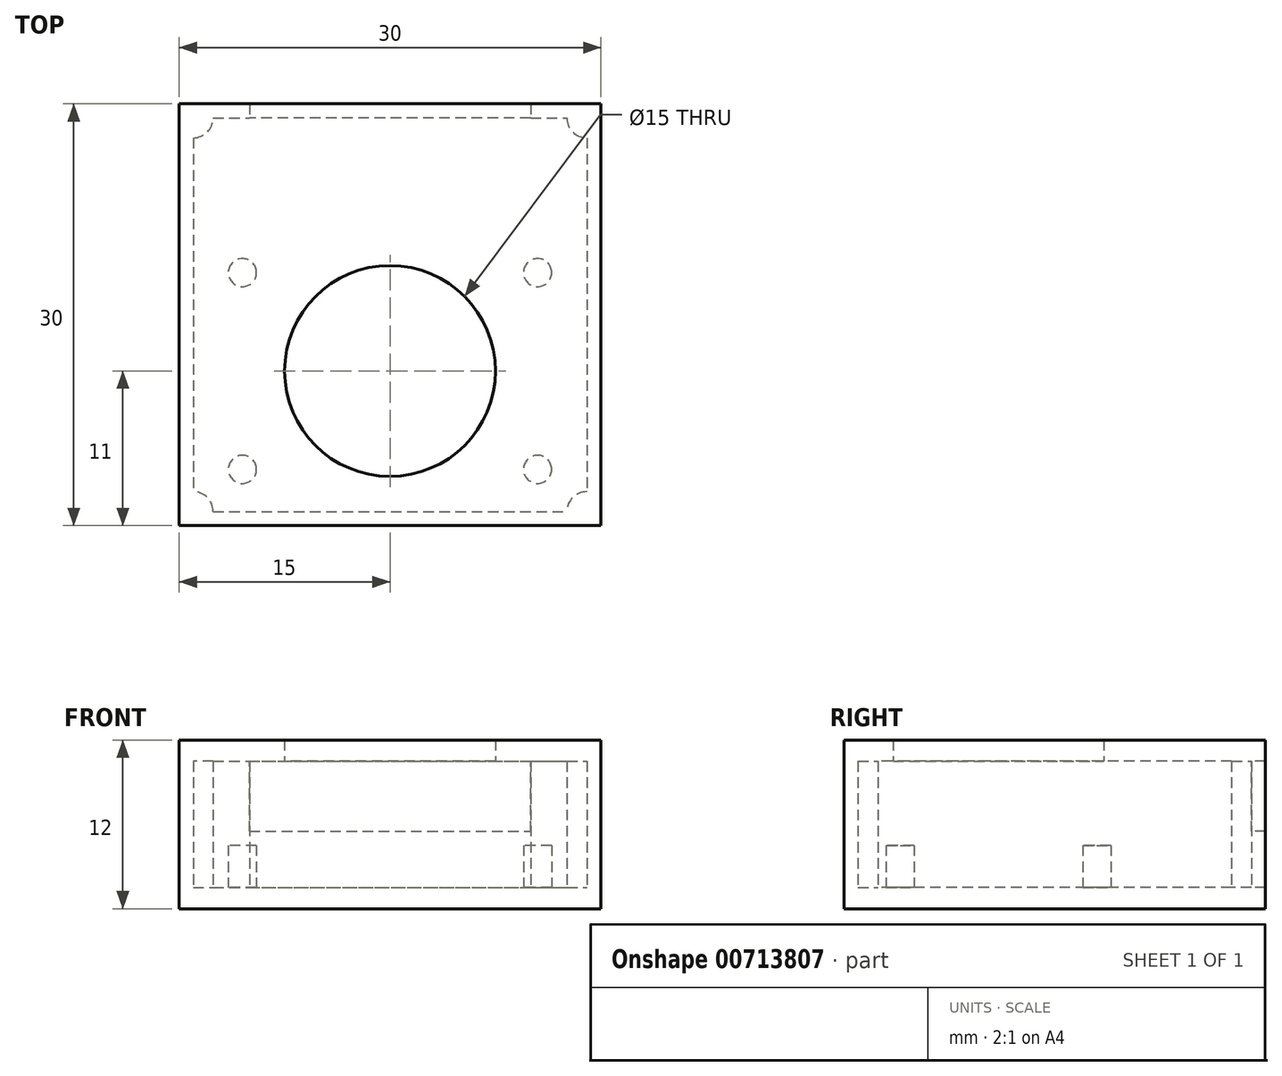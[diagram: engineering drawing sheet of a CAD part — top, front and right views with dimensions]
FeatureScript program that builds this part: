
annotation { "Feature Type Name" : "Feature", "Feature Type Description" : "" }
export const myFeature = defineFeature(function(context is Context, id is Id, definition is map)
    precondition{}
    {
        {
            var Q0;
            Q0=qCreatedBy(makeId("Top.planeOp"),FACE);
            var sketch = newSketch(context, id + "F0", { "sketchPlane" : qUnion([Q0])});
            skLineSegment(sketch, "E0.bottom", {"start": v(0, 0) * mm, "end": v(30, 0) * mm});
            skLineSegment(sketch, "E0.top", {"start": v(0, -30) * mm, "end": v(30, -30) * mm});
            skLineSegment(sketch, "E0.left", {"start": v(0, 0) * mm, "end": v(0, -30) * mm});
            skLineSegment(sketch, "E0.right", {"start": v(30, 0) * mm, "end": v(30, -30) * mm});
            skLineSegment(sketch, "E1.0", {"start": v(1, -1) * mm, "end": v(29, -1) * mm});
            skLineSegment(sketch, "E1.1", {"start": v(1, -1) * mm, "end": v(1, -29) * mm});
            skLineSegment(sketch, "E1.2", {"start": v(1, -29) * mm, "end": v(29, -29) * mm});
            skLineSegment(sketch, "E1.3", {"start": v(29, -1) * mm, "end": v(29, -29) * mm});
            skLineSegment(sketch, "E2", {"start": v(15, -29) * mm, "end": v(15, -1) * mm, "construction": true});
            skPoint(sketch, "E3.start.orphan", {"position": v(1, -19) * mm});
            skPoint(sketch, "E4.start.orphan", {"position": v(29, -19) * mm});
            skLineSegment(sketch, "E5", {"start": v(1, -19) * mm, "end": v(29, -19) * mm, "construction": true});
            skLineSegment(sketch, "E6", {"start": v(1, -12) * mm, "end": v(29, -12) * mm, "construction": true});
            skLineSegment(sketch, "E7", {"start": v(1, -26) * mm, "end": v(29, -26) * mm, "construction": true});
            skLineSegment(sketch, "E8", {"start": v(25.5, -1) * mm, "end": v(25.5, -29) * mm, "construction": true});
            skLineSegment(sketch, "E9", {"start": v(4.5, -1) * mm, "end": v(4.5, -29) * mm, "construction": true});
            skCircle(sketch, "E10", {"center": v(25.5, -12) * mm, "radius": 1 * mm});
            skCircle(sketch, "E11", {"center": v(4.5, -12) * mm, "radius": 1 * mm});
            skCircle(sketch, "E12", {"center": v(4.5, -26) * mm, "radius": 1 * mm});
            skCircle(sketch, "E13", {"center": v(25.5, -26) * mm, "radius": 1 * mm});
            skLineSegment(sketch, "E14", {"start": v(5, 0) * mm, "end": v(5, -1) * mm});
            skLineSegment(sketch, "E15", {"start": v(25, 0) * mm, "end": v(25, -1) * mm});
            skCircle(sketch, "E16", {"center": v(1, -29) * mm, "radius": 1.41 * mm});
            skCircle(sketch, "E17", {"center": v(29, -29) * mm, "radius": 1.41 * mm});
            skCircle(sketch, "E18", {"center": v(29, -1) * mm, "radius": 1.41 * mm});
            skCircle(sketch, "E19", {"center": v(1, -1) * mm, "radius": 1.41 * mm});
            skSolve(sketch);
        }
        {
            var Q0;
            {var subQ0=sQuery(id+"F0.wireOp",EDGE,"E1.1");Q0=makeQuery(id+"F0.imprint","IMPRINT",FACE,{"disambiguationData":[TD([[makeQuery(id+"F0.imprint","IMPRINT",EDGE,{"derivedFrom":subQ0}),1.0]])]});}
            var Q1;
            Q1=makeQuery(id+"F0.imprint","IMPRINT",FACE,{"disambiguationData":[TD([[makeQuery(id+"F0.imprint","IMPRINT",EDGE,{"derivedFrom":sQuery(id+"F0.wireOp",EDGE,"E0.top")}),1.0]])]});
            var Q2;
            Q2=makeQuery(id+"F0.imprint","IMPRINT",FACE,{"disambiguationData":[TD([[makeQuery(id+"F0.imprint","IMPRINT",EDGE,{"derivedFrom":sQuery(id+"F0.wireOp",EDGE,"E11")}),1.0]])]});
            var Q3;
            Q3=makeQuery(id+"F0.imprint","IMPRINT",FACE,{"disambiguationData":[TD([[makeQuery(id+"F0.imprint","IMPRINT",EDGE,{"derivedFrom":sQuery(id+"F0.wireOp",EDGE,"E12")}),1.0]])]});
            var Q4;
            Q4=makeQuery(id+"F0.imprint","IMPRINT",FACE,{"disambiguationData":[TD([[makeQuery(id+"F0.imprint","IMPRINT",EDGE,{"derivedFrom":sQuery(id+"F0.wireOp",EDGE,"E13")}),1.0]])]});
            var Q5;
            Q5=makeQuery(id+"F0.imprint","IMPRINT",FACE,{"disambiguationData":[TD([[makeQuery(id+"F0.imprint","IMPRINT",EDGE,{"derivedFrom":sQuery(id+"F0.wireOp",EDGE,"E10")}),1.0]])]});
            var Q6;
            {var subQ0=sQuery(id+"F0.wireOp",EDGE,"E1.2");var subQ1=sQuery(id+"F0.wireOp",EDGE,"E1.1");var subQ2=makeQuery(id+"F0.imprint","INTERSECT",VERTEX,{"derivedFrom":[subQ1,subQ0]});Q6=makeQuery(id+"F0.imprint","IMPRINT",FACE,{"disambiguationData":[TD([[makeQuery(id+"F0.imprint","IMPRINT",EDGE,{"disambiguationData":[TD([[subQ2,1.0]])],"derivedFrom":subQ1}),-1.0]])]});}
            var Q7;
            {var subQ0=sQuery(id+"F0.wireOp",EDGE,"E19");var subQ1=sQuery(id+"F0.wireOp",EDGE,"E0.left");var subQ2=makeQuery(id+"F0.imprint","INTERSECT",VERTEX,{"derivedFrom":[subQ1,subQ0]});Q7=makeQuery(id+"F0.imprint","IMPRINT",FACE,{"disambiguationData":[TD([[makeQuery(id+"F0.imprint","IMPRINT",EDGE,{"disambiguationData":[TD([[subQ2,-1.0]])],"derivedFrom":subQ1}),1.0]])]});}
            var Q8;
            {var subQ0=sQuery(id+"F0.wireOp",EDGE,"E1.1");var subQ1=sQuery(id+"F0.wireOp",EDGE,"E1.0");var subQ2=makeQuery(id+"F0.imprint","INTERSECT",VERTEX,{"derivedFrom":[subQ1,subQ0]});Q8=makeQuery(id+"F0.imprint","IMPRINT",FACE,{"disambiguationData":[TD([[makeQuery(id+"F0.imprint","IMPRINT",EDGE,{"disambiguationData":[TD([[subQ2,-1.0]])],"derivedFrom":subQ1}),1.0]])]});}
            var Q9;
            {var subQ0=sQuery(id+"F0.wireOp",EDGE,"E14");Q9=makeQuery(id+"F0.imprint","IMPRINT",FACE,{"disambiguationData":[TD([[makeQuery(id+"F0.imprint","IMPRINT",EDGE,{"derivedFrom":subQ0}),1.0]])]});}
            var Q10;
            {var subQ0=sQuery(id+"F0.wireOp",EDGE,"E1.3");var subQ1=sQuery(id+"F0.wireOp",EDGE,"E1.0");var subQ2=makeQuery(id+"F0.imprint","INTERSECT",VERTEX,{"derivedFrom":[subQ1,subQ0]});Q10=makeQuery(id+"F0.imprint","IMPRINT",FACE,{"disambiguationData":[TD([[makeQuery(id+"F0.imprint","IMPRINT",EDGE,{"disambiguationData":[TD([[subQ2,1.0]])],"derivedFrom":subQ1}),1.0]])]});}
            var Q11;
            {var subQ0=sQuery(id+"F0.wireOp",EDGE,"E15");Q11=makeQuery(id+"F0.imprint","IMPRINT",FACE,{"disambiguationData":[TD([[makeQuery(id+"F0.imprint","IMPRINT",EDGE,{"derivedFrom":subQ0}),1.0]])]});}
            var Q12;
            {var subQ0=sQuery(id+"F0.wireOp",EDGE,"E18");var subQ1=sQuery(id+"F0.wireOp",EDGE,"E0.right");var subQ2=makeQuery(id+"F0.imprint","INTERSECT",VERTEX,{"derivedFrom":[subQ1,subQ0]});Q12=makeQuery(id+"F0.imprint","IMPRINT",FACE,{"disambiguationData":[TD([[makeQuery(id+"F0.imprint","IMPRINT",EDGE,{"disambiguationData":[TD([[subQ2,-1.0]])],"derivedFrom":subQ1}),-1.0]])]});}
            var Q13;
            {var subQ0=sQuery(id+"F0.wireOp",EDGE,"E1.3");var subQ1=sQuery(id+"F0.wireOp",EDGE,"E1.2");var subQ2=makeQuery(id+"F0.imprint","INTERSECT",VERTEX,{"derivedFrom":[subQ1,subQ0]});Q13=makeQuery(id+"F0.imprint","IMPRINT",FACE,{"disambiguationData":[TD([[makeQuery(id+"F0.imprint","IMPRINT",EDGE,{"disambiguationData":[TD([[subQ2,1.0]])],"derivedFrom":subQ1}),-1.0]])]});}
            var Q14;
            Q14=makeQuery(id+"F0.imprint","IMPRINT",FACE,{"disambiguationData":[TD([[makeQuery(id+"F0.imprint","IMPRINT",EDGE,{"derivedFrom":sQuery(id+"F0.wireOp",EDGE,"E10")}),-1.0]])]});
            var Q15;
            {var subQ0=sQuery(id+"F0.wireOp",EDGE,"E1.3");var subQ1=sQuery(id+"F0.wireOp",EDGE,"E1.2");var subQ2=makeQuery(id+"F0.imprint","INTERSECT",VERTEX,{"derivedFrom":[subQ1,subQ0]});Q15=makeQuery(id+"F0.imprint","IMPRINT",FACE,{"disambiguationData":[TD([[makeQuery(id+"F0.imprint","IMPRINT",EDGE,{"disambiguationData":[TD([[subQ2,1.0]])],"derivedFrom":subQ1}),1.0]])]});}
            var Q16;
            {var subQ0=sQuery(id+"F0.wireOp",EDGE,"E14");Q16=makeQuery(id+"F0.imprint","IMPRINT",FACE,{"disambiguationData":[TD([[makeQuery(id+"F0.imprint","IMPRINT",EDGE,{"derivedFrom":subQ0}),-1.0]])]});}
            var Q17;
            {var subQ0=sQuery(id+"F0.wireOp",EDGE,"E1.3");var subQ1=sQuery(id+"F0.wireOp",EDGE,"E1.0");var subQ2=makeQuery(id+"F0.imprint","INTERSECT",VERTEX,{"derivedFrom":[subQ1,subQ0]});Q17=makeQuery(id+"F0.imprint","IMPRINT",FACE,{"disambiguationData":[TD([[makeQuery(id+"F0.imprint","IMPRINT",EDGE,{"disambiguationData":[TD([[subQ2,1.0]])],"derivedFrom":subQ1}),-1.0]])]});}
            extrude(context, id + "F1", {"entities" : qUnion([Q0, Q1, Q2, Q3, Q4, Q5, Q6, Q7, Q8, Q9, Q10, Q11, Q12, Q13, Q14, Q15, Q16, Q17]), "oppositeDirection" : true, "depth" : 1.5 * mm, "offsetDistance" : 25 * mm});
        }
        {
            var Q0;
            Q0=makeQuery(id+"F0.imprint","IMPRINT",FACE,{"disambiguationData":[TD([[makeQuery(id+"F0.imprint","IMPRINT",EDGE,{"derivedFrom":sQuery(id+"F0.wireOp",EDGE,"E11")}),1.0]])]});
            var Q1;
            Q1=makeQuery(id+"F0.imprint","IMPRINT",FACE,{"disambiguationData":[TD([[makeQuery(id+"F0.imprint","IMPRINT",EDGE,{"derivedFrom":sQuery(id+"F0.wireOp",EDGE,"E10")}),1.0]])]});
            var Q2;
            Q2=makeQuery(id+"F0.imprint","IMPRINT",FACE,{"disambiguationData":[TD([[makeQuery(id+"F0.imprint","IMPRINT",EDGE,{"derivedFrom":sQuery(id+"F0.wireOp",EDGE,"E13")}),1.0]])]});
            var Q3;
            Q3=makeQuery(id+"F0.imprint","IMPRINT",FACE,{"disambiguationData":[TD([[makeQuery(id+"F0.imprint","IMPRINT",EDGE,{"derivedFrom":sQuery(id+"F0.wireOp",EDGE,"E12")}),1.0]])]});
            extrude(context, id + "F2", {"entities" : qUnion([Q0, Q1, Q2, Q3]), "operationType" : NewBodyOperationType.ADD, "depth" : 3 * mm, "offsetDistance" : 25 * mm});
        }
        {
            var Q0;
            Q0=makeQuery(id+"F0.imprint","IMPRINT",FACE,{"disambiguationData":[TD([[makeQuery(id+"F0.imprint","IMPRINT",EDGE,{"derivedFrom":sQuery(id+"F0.wireOp",EDGE,"E0.top")}),1.0]])]});
            var Q1;
            {var subQ0=sQuery(id+"F0.wireOp",EDGE,"E1.3");var subQ1=sQuery(id+"F0.wireOp",EDGE,"E1.2");var subQ2=makeQuery(id+"F0.imprint","INTERSECT",VERTEX,{"derivedFrom":[subQ1,subQ0]});Q1=makeQuery(id+"F0.imprint","IMPRINT",FACE,{"disambiguationData":[TD([[makeQuery(id+"F0.imprint","IMPRINT",EDGE,{"disambiguationData":[TD([[subQ2,1.0]])],"derivedFrom":subQ1}),-1.0]])]});}
            var Q2;
            {var subQ0=sQuery(id+"F0.wireOp",EDGE,"E18");var subQ1=sQuery(id+"F0.wireOp",EDGE,"E0.right");var subQ2=makeQuery(id+"F0.imprint","INTERSECT",VERTEX,{"derivedFrom":[subQ1,subQ0]});Q2=makeQuery(id+"F0.imprint","IMPRINT",FACE,{"disambiguationData":[TD([[makeQuery(id+"F0.imprint","IMPRINT",EDGE,{"disambiguationData":[TD([[subQ2,-1.0]])],"derivedFrom":subQ1}),-1.0]])]});}
            var Q3;
            {var subQ0=sQuery(id+"F0.wireOp",EDGE,"E1.3");var subQ1=sQuery(id+"F0.wireOp",EDGE,"E1.0");var subQ2=makeQuery(id+"F0.imprint","INTERSECT",VERTEX,{"derivedFrom":[subQ1,subQ0]});Q3=makeQuery(id+"F0.imprint","IMPRINT",FACE,{"disambiguationData":[TD([[makeQuery(id+"F0.imprint","IMPRINT",EDGE,{"disambiguationData":[TD([[subQ2,1.0]])],"derivedFrom":subQ1}),1.0]])]});}
            var Q4;
            {var subQ0=sQuery(id+"F0.wireOp",EDGE,"E15");Q4=makeQuery(id+"F0.imprint","IMPRINT",FACE,{"disambiguationData":[TD([[makeQuery(id+"F0.imprint","IMPRINT",EDGE,{"derivedFrom":subQ0}),1.0]])]});}
            var Q5;
            {var subQ0=sQuery(id+"F0.wireOp",EDGE,"E14");Q5=makeQuery(id+"F0.imprint","IMPRINT",FACE,{"disambiguationData":[TD([[makeQuery(id+"F0.imprint","IMPRINT",EDGE,{"derivedFrom":subQ0}),-1.0]])]});}
            var Q6;
            {var subQ0=sQuery(id+"F0.wireOp",EDGE,"E1.1");var subQ1=sQuery(id+"F0.wireOp",EDGE,"E1.0");var subQ2=makeQuery(id+"F0.imprint","INTERSECT",VERTEX,{"derivedFrom":[subQ1,subQ0]});Q6=makeQuery(id+"F0.imprint","IMPRINT",FACE,{"disambiguationData":[TD([[makeQuery(id+"F0.imprint","IMPRINT",EDGE,{"disambiguationData":[TD([[subQ2,-1.0]])],"derivedFrom":subQ1}),1.0]])]});}
            var Q7;
            {var subQ0=sQuery(id+"F0.wireOp",EDGE,"E19");var subQ1=sQuery(id+"F0.wireOp",EDGE,"E0.left");var subQ2=makeQuery(id+"F0.imprint","INTERSECT",VERTEX,{"derivedFrom":[subQ1,subQ0]});Q7=makeQuery(id+"F0.imprint","IMPRINT",FACE,{"disambiguationData":[TD([[makeQuery(id+"F0.imprint","IMPRINT",EDGE,{"disambiguationData":[TD([[subQ2,-1.0]])],"derivedFrom":subQ1}),1.0]])]});}
            var Q8;
            {var subQ0=sQuery(id+"F0.wireOp",EDGE,"E1.2");var subQ1=sQuery(id+"F0.wireOp",EDGE,"E1.1");var subQ2=makeQuery(id+"F0.imprint","INTERSECT",VERTEX,{"derivedFrom":[subQ1,subQ0]});Q8=makeQuery(id+"F0.imprint","IMPRINT",FACE,{"disambiguationData":[TD([[makeQuery(id+"F0.imprint","IMPRINT",EDGE,{"disambiguationData":[TD([[subQ2,1.0]])],"derivedFrom":subQ1}),-1.0]])]});}
            extrude(context, id + "F3", {"entities" : qUnion([Q0, Q1, Q2, Q3, Q4, Q5, Q6, Q7, Q8]), "operationType" : NewBodyOperationType.ADD, "depth" : 9 * mm, "offsetDistance" : 25 * mm});
        }
        {
            var Q0;
            Q0=makeQuery(id+"F3.opExtrude","CAP_FACE",FACE,{"disambiguationData":[OSD([sQuery(id+"F0.wireOp",EDGE,"E0.bottom"),sQuery(id+"F0.wireOp",EDGE,"E0.top"),sQuery(id+"F0.wireOp",EDGE,"E0.left"),sQuery(id+"F0.wireOp",EDGE,"E0.right"),sQuery(id+"F0.wireOp",EDGE,"E1.0"),sQuery(id+"F0.wireOp",EDGE,"E1.1"),sQuery(id+"F0.wireOp",EDGE,"E1.2"),sQuery(id+"F0.wireOp",EDGE,"E1.3"),sQuery(id+"F0.wireOp",EDGE,"E14"),sQuery(id+"F0.wireOp",EDGE,"E15")])],"isStart":false});
            var sketch = newSketch(context, id + "F4", { "sketchPlane" : qUnion([Q0])});
            skLineSegment(sketch, "E20.0", {"start": v(25, 0) * mm, "end": v(30, 0) * mm});
            skLineSegment(sketch, "E21.0", {"start": v(30, 0) * mm, "end": v(30, -30) * mm});
            skLineSegment(sketch, "E22.0", {"start": v(0, -30) * mm, "end": v(30, -30) * mm});
            skLineSegment(sketch, "E23.0", {"start": v(0, 0) * mm, "end": v(0, -30) * mm});
            skLineSegment(sketch, "E24.0", {"start": v(0, 0) * mm, "end": v(5, 0) * mm});
            skPoint(sketch, "E25.0", {"position": v(15, -19) * mm});
            skLineSegment(sketch, "E26", {"start": v(5, 0) * mm, "end": v(25, 0) * mm});
            skCircle(sketch, "E27", {"center": v(15, -19) * mm, "radius": 7.5 * mm});
            skArc(sketch, "E28.0.0", {"start": v(2.41, -1) * mm, "mid": v(2, -2) * mm, "end": v(1, -2.41) * mm});
            skLineSegment(sketch, "E28.0.1", {"start": v(1, -2.41) * mm, "end": v(1, -27.59) * mm});
            skArc(sketch, "E28.0.2", {"start": v(1, -27.59) * mm, "mid": v(2, -28) * mm, "end": v(2.41, -29) * mm});
            skLineSegment(sketch, "E28.0.3", {"start": v(2.41, -29) * mm, "end": v(27.59, -29) * mm});
            skArc(sketch, "E28.0.4", {"start": v(27.59, -29) * mm, "mid": v(28, -28) * mm, "end": v(29, -27.59) * mm});
            skLineSegment(sketch, "E28.0.5", {"start": v(29, -27.59) * mm, "end": v(29, -2.41) * mm});
            skArc(sketch, "E28.0.6", {"start": v(29, -2.41) * mm, "mid": v(28, -2) * mm, "end": v(27.59, -1) * mm});
            skLineSegment(sketch, "E28.0.7", {"start": v(27.59, -1) * mm, "end": v(25, -1) * mm});
            skLineSegment(sketch, "E28.0.8", {"start": v(25, -1) * mm, "end": v(5, -1) * mm});
            skLineSegment(sketch, "E28.0.9", {"start": v(5, -1) * mm, "end": v(2.41, -1) * mm});
            skLineSegment(sketch, "E29.0", {"start": v(1, -1) * mm, "end": v(5, -1) * mm});
            skLineSegment(sketch, "E30.0", {"start": v(1, -1) * mm, "end": v(1, -29) * mm});
            skLineSegment(sketch, "E31.0", {"start": v(29, -1) * mm, "end": v(29, -29) * mm});
            skLineSegment(sketch, "E32.0", {"start": v(25, -1) * mm, "end": v(29, -1) * mm});
            skLineSegment(sketch, "E33.0", {"start": v(1, -29) * mm, "end": v(29, -29) * mm});
            skLineSegment(sketch, "E34.0.0", {"start": v(29, -29) * mm, "end": v(1, -29) * mm});
            skLineSegment(sketch, "E34.0.1", {"start": v(1, -29) * mm, "end": v(1, -1) * mm});
            skLineSegment(sketch, "E34.0.3", {"start": v(5, -1) * mm, "end": v(5, 0) * mm});
            skLineSegment(sketch, "E34.0.4", {"start": v(5, 0) * mm, "end": v(0, 0) * mm});
            skLineSegment(sketch, "E34.0.7", {"start": v(30, -30) * mm, "end": v(30, 0) * mm});
            skLineSegment(sketch, "E34.0.8", {"start": v(30, 0) * mm, "end": v(25, 0) * mm});
            skLineSegment(sketch, "E34.0.9", {"start": v(25, 0) * mm, "end": v(25, -1) * mm});
            skSolve(sketch);
        }
        {
            var Q0;
            Q0=makeQuery(id+"F4.imprint","IMPRINT",FACE,{"disambiguationData":[TD([[makeQuery(id+"F4.imprint","IMPRINT",EDGE,{"derivedFrom":sQuery(id+"F4.wireOp",EDGE,"E26")}),-1.0]])]});
            var Q1;
            Q1=makeQuery(id+"F4.imprint","IMPRINT",FACE,{"disambiguationData":[TD([[makeQuery(id+"F4.imprint","IMPRINT",EDGE,{"derivedFrom":sQuery(id+"F4.wireOp",EDGE,"E20.0")}),-1.0]])]});
            var Q2;
            {var subQ0=sQuery(id+"F4.wireOp",EDGE,"E34.0.3");Q2=makeQuery(id+"F4.imprint","IMPRINT",FACE,{"disambiguationData":[TD([[makeQuery(id+"F4.imprint","IMPRINT",EDGE,{"derivedFrom":subQ0}),-1.0]])]});}
            var Q3;
            Q3=makeQuery(id+"F4.imprint","IMPRINT",FACE,{"disambiguationData":[TD([[makeQuery(id+"F4.imprint","IMPRINT",EDGE,{"derivedFrom":sQuery(id+"F4.wireOp",EDGE,"E27")}),-1.0]])]});
            extrude(context, id + "F5", {"entities" : qUnion([Q0, Q1, Q2, Q3]), "depth" : 1.5 * mm, "offsetDistance" : 25 * mm});
        }
        {
            var Q0;
            {var subQ0=sQuery(id+"F0.wireOp",EDGE,"E1.1");var subQ1=sQuery(id+"F0.wireOp",EDGE,"E1.0");var subQ2=makeQuery(id+"F0.imprint","INTERSECT",VERTEX,{"derivedFrom":[subQ1,subQ0]});Q0=makeQuery(id+"F0.imprint","IMPRINT",FACE,{"disambiguationData":[TD([[makeQuery(id+"F0.imprint","IMPRINT",EDGE,{"disambiguationData":[TD([[subQ2,-1.0]])],"derivedFrom":subQ1}),-1.0]])]});}
            var Q1;
            {var subQ0=sQuery(id+"F0.wireOp",EDGE,"E1.2");var subQ1=sQuery(id+"F0.wireOp",EDGE,"E1.1");var subQ2=makeQuery(id+"F0.imprint","INTERSECT",VERTEX,{"derivedFrom":[subQ1,subQ0]});Q1=makeQuery(id+"F0.imprint","IMPRINT",FACE,{"disambiguationData":[TD([[makeQuery(id+"F0.imprint","IMPRINT",EDGE,{"disambiguationData":[TD([[subQ2,1.0]])],"derivedFrom":subQ1}),1.0]])]});}
            var Q2;
            {var subQ0=sQuery(id+"F0.wireOp",EDGE,"E1.3");var subQ1=sQuery(id+"F0.wireOp",EDGE,"E1.2");var subQ2=makeQuery(id+"F0.imprint","INTERSECT",VERTEX,{"derivedFrom":[subQ1,subQ0]});Q2=makeQuery(id+"F0.imprint","IMPRINT",FACE,{"disambiguationData":[TD([[makeQuery(id+"F0.imprint","IMPRINT",EDGE,{"disambiguationData":[TD([[subQ2,1.0]])],"derivedFrom":subQ1}),1.0]])]});}
            var Q3;
            {var subQ0=sQuery(id+"F0.wireOp",EDGE,"E1.3");var subQ1=sQuery(id+"F0.wireOp",EDGE,"E1.0");var subQ2=makeQuery(id+"F0.imprint","INTERSECT",VERTEX,{"derivedFrom":[subQ1,subQ0]});Q3=makeQuery(id+"F0.imprint","IMPRINT",FACE,{"disambiguationData":[TD([[makeQuery(id+"F0.imprint","IMPRINT",EDGE,{"disambiguationData":[TD([[subQ2,1.0]])],"derivedFrom":subQ1}),-1.0]])]});}
            extrude(context, id + "F6", {"entities" : qUnion([Q0, Q1, Q2, Q3]), "operationType" : NewBodyOperationType.ADD, "depth" : 10.5 * mm, "offsetDistance" : 25 * mm});
        }
        {
            var Q0;
            Q0=makeQuery(id+"F6.opExtrude","CAP_FACE",FACE,{"disambiguationData":[OSD([sQuery(id+"F0.wireOp",EDGE,"E1.0"),sQuery(id+"F0.wireOp",EDGE,"E1.3"),sQuery(id+"F0.wireOp",EDGE,"E18")])],"isStart":false});
            var Q1;
            Q1=makeQuery(id+"F6.opExtrude","CAP_FACE",FACE,{"disambiguationData":[OSD([sQuery(id+"F0.wireOp",EDGE,"E1.0"),sQuery(id+"F0.wireOp",EDGE,"E1.1"),sQuery(id+"F0.wireOp",EDGE,"E19")])],"isStart":false});
            var Q2;
            Q2=makeQuery(id+"F6.opExtrude","CAP_FACE",FACE,{"disambiguationData":[OSD([sQuery(id+"F0.wireOp",EDGE,"E1.1"),sQuery(id+"F0.wireOp",EDGE,"E1.2"),sQuery(id+"F0.wireOp",EDGE,"E16")])],"isStart":false});
            var Q3;
            Q3=makeQuery(id+"F6.opExtrude","CAP_FACE",FACE,{"disambiguationData":[OSD([sQuery(id+"F0.wireOp",EDGE,"E1.2"),sQuery(id+"F0.wireOp",EDGE,"E1.3"),sQuery(id+"F0.wireOp",EDGE,"E17")])],"isStart":false});
            extrude(context, id + "F7", {"entities" : qUnion([Q0, Q1, Q2, Q3]), "operationType" : NewBodyOperationType.REMOVE, "depth" : 25 * mm, "offsetDistance" : 25 * mm});
        }
        {
            var Q0;
            Q0=makeQuery(id+"F4.imprint","IMPRINT",FACE,{"disambiguationData":[TD([[makeQuery(id+"F4.imprint","IMPRINT",EDGE,{"derivedFrom":sQuery(id+"F4.wireOp",EDGE,"E26")}),-1.0]])]});
            extrude(context, id + "F8", {"entities" : qUnion([Q0]), "oppositeDirection" : true, "depth" : 5 * mm, "offsetDistance" : 25 * mm});
        }
        {
            var Q0;
            Q0=qCreatedBy(makeId("Right.planeOp"),FACE);
            var sketch = newSketch(context, id + "F9", { "sketchPlane" : qUnion([Q0])});
            skArc(sketch, "E35", {"start": v(25.23, -40.78) * mm, "mid": v(21.37, -35.91) * mm, "end": v(15.75, -38.54) * mm});
            skLineSegment(sketch, "E36", {"start": v(15.23, -40.78) * mm, "end": v(5.5, -40.78) * mm});
            skLineSegment(sketch, "E37", {"start": v(5.5, -40.78) * mm, "end": v(5.5, -36.15) * mm});
            skLineSegment(sketch, "E38", {"start": v(9.7, -36.15) * mm, "end": v(9.7, -38.54) * mm});
            skLineSegment(sketch, "E39", {"start": v(9.7, -38.54) * mm, "end": v(15.75, -38.54) * mm});
            skLineSegment(sketch, "E40", {"start": v(15.23, -40.78) * mm, "end": v(25.23, -40.78) * mm});
            skLineSegment(sketch, "E41", {"start": v(5.5, -36.15) * mm, "end": v(9.7, -36.15) * mm});
            skSolve(sketch);
        }
        {
            var Q0;
            Q0=qCreatedBy(makeId("Right.planeOp"),FACE);
            var sketch = newSketch(context, id + "F10", { "sketchPlane" : qUnion([Q0])});
            skPoint(sketch, "E42.0", {"position": v(20.23, -40.78) * mm});
            skArc(sketch, "E43.1", {"start": v(25.33, -40.78) * mm, "mid": v(23.36, -36.76) * mm, "end": v(18.99, -35.83) * mm});
            skLineSegment(sketch, "E44", {"start": v(18.99, -35.83) * mm, "end": v(18.99, -34.79) * mm});
            skLineSegment(sketch, "E45", {"start": v(18.99, -34.79) * mm, "end": v(26.24, -34.79) * mm});
            skLineSegment(sketch, "E46", {"start": v(26.24, -34.79) * mm, "end": v(26.24, -38.87) * mm});
            skLineSegment(sketch, "E47", {"start": v(26.24, -40.78) * mm, "end": v(30.27, -40.78) * mm});
            skLineSegment(sketch, "E48", {"start": v(30.27, -40.78) * mm, "end": v(30.27, -38.87) * mm});
            skLineSegment(sketch, "E49", {"start": v(30.27, -38.87) * mm, "end": v(26.24, -38.87) * mm});
            skLineSegment(sketch, "E50", {"start": v(26.24, -40.78) * mm, "end": v(25.33, -40.78) * mm});
            skPoint(sketch, "E51.orphan", {"position": v(15.23, -40.78) * mm});
            skPoint(sketch, "E52.0.end.orphan", {"position": v(5.5, -40.78) * mm});
            skPoint(sketch, "E53.0.end.orphan", {"position": v(15.75, -38.54) * mm});
            skPoint(sketch, "E53.0.start.orphan", {"position": v(9.7, -38.54) * mm});
            skPoint(sketch, "E54.0.start.orphan", {"position": v(25.23, -40.78) * mm});
            skSolve(sketch);
        }
        {
            var Q0;
            Q0=makeQuery(id+"F9.imprint","IMPRINT",FACE,{"disambiguationData":[TD([[makeQuery(id+"F9.imprint","IMPRINT",EDGE,{"derivedFrom":sQuery(id+"F9.wireOp",EDGE,"E35")}),1.0]])]});
            var Q1;
            Q1=sQuery(id+"F9.wireOp",EDGE,"E40");
            revolve(context, id + "F11", {"surfaceOperationType" : NewSurfaceOperationType.NEW, "entities" : qUnion([Q0]), "axis" : qUnion([Q1]), "revolveType" : RevolveType.FULL});
        }
        {
            var Q0;
            Q0=makeQuery(id+"F10.imprint","IMPRINT",FACE,{"disambiguationData":[TD([[makeQuery(id+"F10.imprint","IMPRINT",EDGE,{"derivedFrom":sQuery(id+"F10.wireOp",EDGE,"E43.1")}),-1.0]])]});
            var Q1;
            Q1=sQuery(id+"F10.wireOp",EDGE,"E47");
            revolve(context, id + "F12", {"surfaceOperationType" : NewSurfaceOperationType.NEW, "entities" : qUnion([Q0]), "axis" : qUnion([Q1]), "revolveType" : RevolveType.FULL});
        }
        {
            var Q0;
            Q0=makeQuery(id+"F12.opRevolve","SWEPT_EDGE",EDGE,{"disambiguationData":[OSD([sQuery(id+"F10.wireOp",EDGE,"E46"),sQuery(id+"F10.wireOp",EDGE,"E49")])]});
            fillet(context, id + "F13", {"entities" : qUnion([Q0]), "radius" : 2 * mm, "tangentPropagation" : true, "allowEdgeOverflow" : false});
        }
        {
            var Q0;
            Q0=makeQuery(id+"F11.opRevolve","SWEPT_BODY",BODY,{"disambiguationData":[OSD([sQuery(id+"F9.wireOp",EDGE,"E35"),sQuery(id+"F9.wireOp",EDGE,"E36"),sQuery(id+"F9.wireOp",EDGE,"E37"),sQuery(id+"F9.wireOp",EDGE,"E38"),sQuery(id+"F9.wireOp",EDGE,"E39"),sQuery(id+"F9.wireOp",EDGE,"E40"),sQuery(id+"F9.wireOp",EDGE,"E41")])]});
            deleteBodies(context, id + "F14", {"entities" : qUnion([Q0])});
        }
        {
            var Q0;
            Q0=makeQuery(id+"F12.opRevolve","SWEPT_BODY",BODY,{"disambiguationData":[OSD([sQuery(id+"F10.wireOp",EDGE,"E43.1"),sQuery(id+"F10.wireOp",EDGE,"E44"),sQuery(id+"F10.wireOp",EDGE,"E45"),sQuery(id+"F10.wireOp",EDGE,"E46"),sQuery(id+"F10.wireOp",EDGE,"E47"),sQuery(id+"F10.wireOp",EDGE,"E48"),sQuery(id+"F10.wireOp",EDGE,"E49"),sQuery(id+"F10.wireOp",EDGE,"E50")])]});
            deleteBodies(context, id + "F15", {"entities" : qUnion([Q0])});
        }
    });
